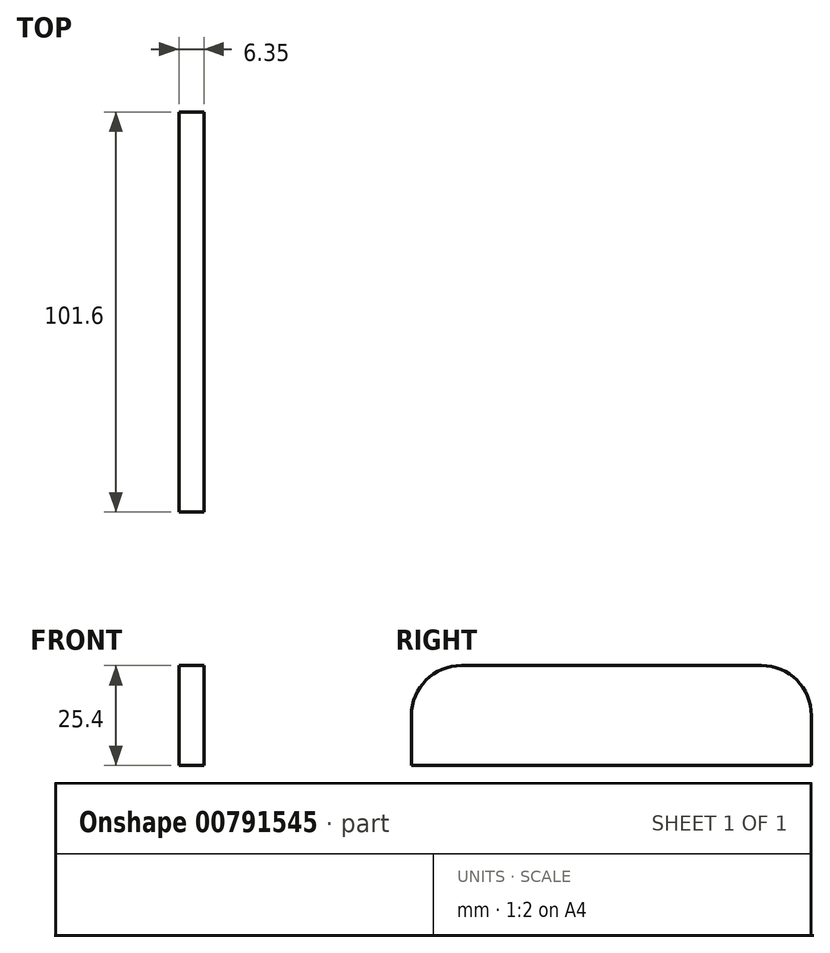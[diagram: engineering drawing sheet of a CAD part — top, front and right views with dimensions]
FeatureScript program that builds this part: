
annotation { "Feature Type Name" : "Feature", "Feature Type Description" : "" }
export const myFeature = defineFeature(function(context is Context, id is Id, definition is map)
    precondition{}
    {
        {
            var Q0;
            Q0=qCreatedBy(makeId("Right.planeOp"),FACE);
            var sketch = newSketch(context, id + "F0", { "sketchPlane" : qUnion([Q0])});
            skLineSegment(sketch, "E0.bottom", {"start": v(-41.57, 0) * mm, "end": v(60.03, 0) * mm});
            skLineSegment(sketch, "E0.top", {"start": v(-28.87, 25.4) * mm, "end": v(47.33, 25.4) * mm});
            skLineSegment(sketch, "E0.left", {"start": v(-41.57, 0) * mm, "end": v(-41.57, 12.7) * mm});
            skLineSegment(sketch, "E0.right", {"start": v(60.03, 0) * mm, "end": v(60.03, 12.7) * mm});
            skPoint(sketch, "E1.visualSharp", {"position": v(-41.57, 25.4) * mm});
            skArc(sketch, "E1.filletArc", {"start": v(-28.87, 25.4) * mm, "mid": v(-37.85, 21.68) * mm, "end": v(-41.57, 12.7) * mm});
            skPoint(sketch, "E2.visualSharp", {"position": v(60.03, 25.4) * mm});
            skArc(sketch, "E2.filletArc", {"start": v(60.03, 12.7) * mm, "mid": v(56.3, 21.68) * mm, "end": v(47.33, 25.4) * mm});
            skSolve(sketch);
        }
        {
            var Q0;
            Q0=makeQuery(id+"F0.imprint","IMPRINT",FACE,{"disambiguationData":[TD([[makeQuery(id+"F0.imprint","IMPRINT",EDGE,{"derivedFrom":sQuery(id+"F0.wireOp",EDGE,"E0.bottom")}),1.0]])]});
            extrude(context, id + "F1", {"entities" : qUnion([Q0]), "depth" : 6.35 * mm, "offsetDistance" : 25.4 * mm});
        }
    });
